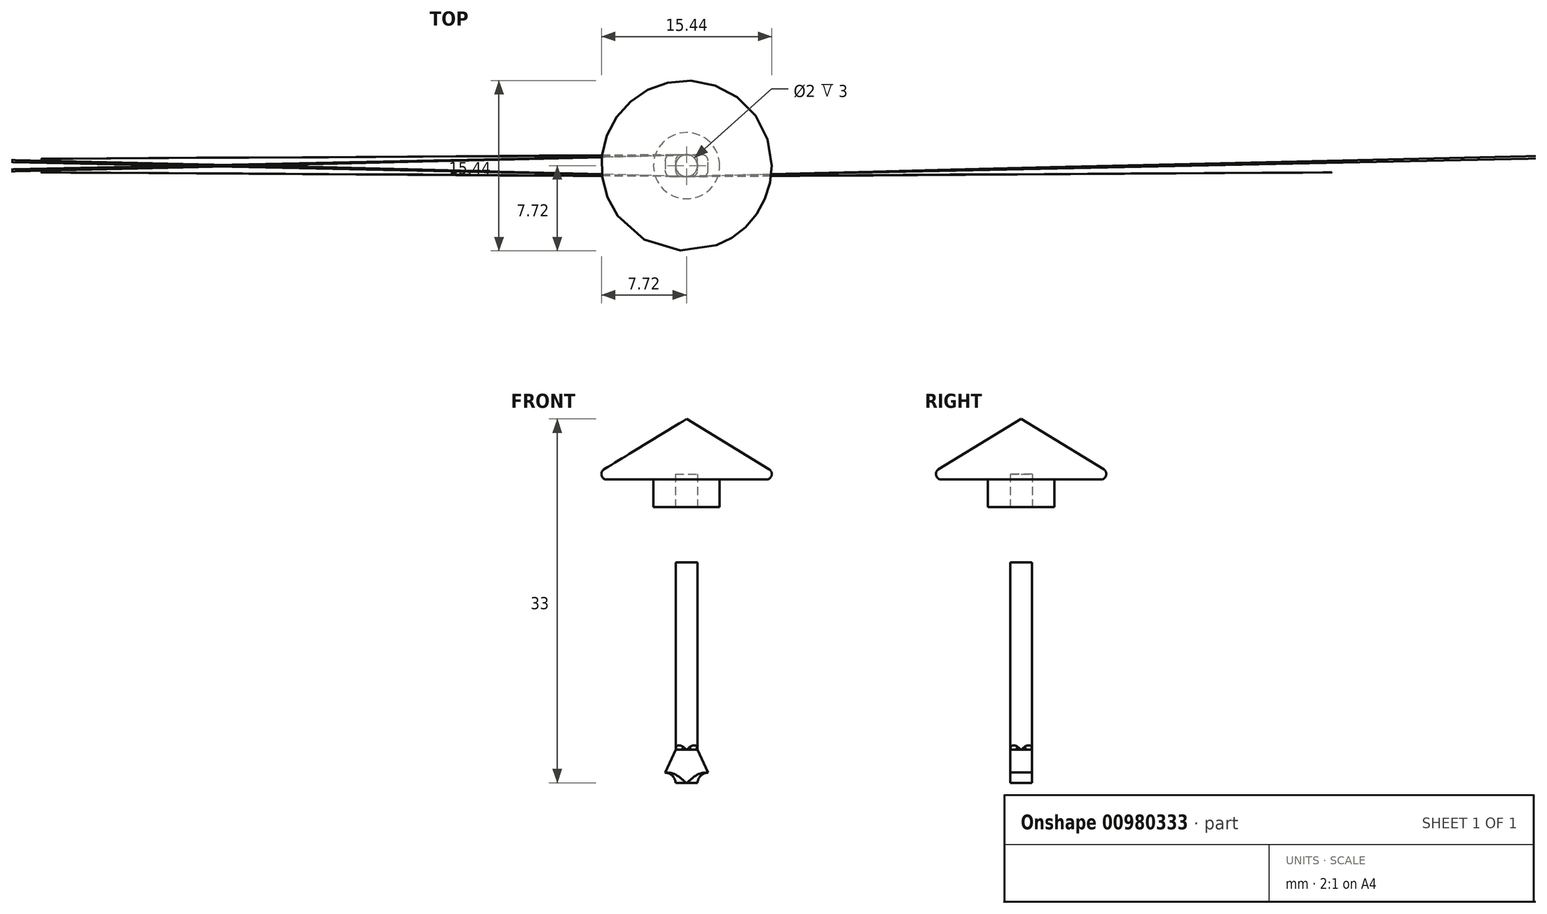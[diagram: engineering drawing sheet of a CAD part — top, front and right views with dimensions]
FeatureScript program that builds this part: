
annotation { "Feature Type Name" : "Feature", "Feature Type Description" : "" }
export const myFeature = defineFeature(function(context is Context, id is Id, definition is map)
    precondition{}
    {
        {
            var Q0;
            Q0=qCreatedBy(makeId("Front.planeOp"),FACE);
            var sketch = newSketch(context, id + "F0", { "sketchPlane" : qUnion([Q0])});
            skLineSegment(sketch, "E0", {"start": v(0, 8) * mm, "end": v(-9, 2.5) * mm});
            skLineSegment(sketch, "E1", {"start": v(-9, 2.5) * mm, "end": v(-3, 2.5) * mm});
            skLineSegment(sketch, "E2", {"start": v(-3, 2.5) * mm, "end": v(-3, 0) * mm});
            skLineSegment(sketch, "E3", {"start": v(-3, 0) * mm, "end": v(0, 0) * mm});
            skLineSegment(sketch, "E4", {"start": v(0, 0) * mm, "end": v(0, 8) * mm});
            skSolve(sketch);
        }
        {
            var Q0;
            Q0=makeQuery(id+"F0.imprint","IMPRINT",FACE,{"disambiguationData":[TD([[makeQuery(id+"F0.imprint","IMPRINT",EDGE,{"derivedFrom":sQuery(id+"F0.wireOp",EDGE,"E0")}),1.0]])]});
            var Q1;
            Q1=sQuery(id+"F0.wireOp",EDGE,"E4");
            revolve(context, id + "F1", {"surfaceOperationType" : NewSurfaceOperationType.NEW, "entities" : qUnion([Q0]), "axis" : qUnion([Q1]), "revolveType" : RevolveType.FULL});
        }
        {
            var Q0;
            Q0=makeQuery(id+"F1.opRevolve","SWEPT_EDGE",EDGE,{"disambiguationData":[OSD([sQuery(id+"F0.wireOp",EDGE,"E0"),sQuery(id+"F0.wireOp",EDGE,"E1")])]});
            var Q1;
            Q1=makeQuery(id+"F1.opRevolve","SWEPT_FACE",FACE,{"disambiguationData":[OSD([sQuery(id+"F0.wireOp",EDGE,"E0")])]});
            fillet(context, id + "F2", {"entities" : qUnion([Q0, Q1]), "radius" : 0.5 * mm, "tangentPropagation" : true, "allowEdgeOverflow" : false});
        }
        {
            var Q0;
            Q0=makeQuery(id+"F1.opRevolve","SWEPT_FACE",FACE,{"disambiguationData":[OSD([sQuery(id+"F0.wireOp",EDGE,"E3")])]});
            var sketch = newSketch(context, id + "F3", { "sketchPlane" : qUnion([Q0])});
            skCircle(sketch, "E5", {"center": v(0, 0) * mm, "radius": 1 * mm});
            skSolve(sketch);
        }
        {
            var Q0;
            Q0=makeQuery(id+"F3.imprint","IMPRINT",FACE,{"disambiguationData":[TD([[makeQuery(id+"F3.imprint","IMPRINT",EDGE,{"derivedFrom":sQuery(id+"F3.wireOp",EDGE,"E5")}),1.0]])]});
            extrude(context, id + "F4", {"entities" : qUnion([Q0]), "operationType" : NewBodyOperationType.REMOVE, "oppositeDirection" : true, "depth" : 3 * mm, "offsetDistance" : 25 * mm});
        }
        {
            var Q0;
            Q0=makeQuery(id+"F3.imprint","IMPRINT",FACE,{"disambiguationData":[TD([[makeQuery(id+"F3.imprint","IMPRINT",EDGE,{"derivedFrom":sQuery(id+"F3.wireOp",EDGE,"E5")}),-1.0]])]});
            cPlane(context, id + "F5", {"entities" : qUnion([Q0]), "cplaneType" : CPlaneType.OFFSET, "offset" : 5 * mm, "width" : 150 * mm, "height" : 150 * mm});
        }
        {
            var Q0;
            Q0=qCreatedBy(id+"F5.planeOp",FACE);
            var sketch = newSketch(context, id + "F6", { "sketchPlane" : qUnion([Q0])});
            skCircle(sketch, "E6", {"center": v(0, 0) * mm, "radius": 0.99 * mm});
            skSolve(sketch);
        }
        {
            var Q0;
            Q0 = qSketchRegion(id + "F6", true);
            extrude(context, id + "F7", {"entities" : qUnion([Q0]), "depth" : 20 * mm, "offsetDistance" : 25 * mm});
        }
        {
            var Q0;
            Q0=qCreatedBy(makeId("Front.planeOp"),FACE);
            var sketch = newSketch(context, id + "F8", { "sketchPlane" : qUnion([Q0])});
            skLineSegment(sketch, "E7", {"start": v(1, -5) * mm, "end": v(1, -25) * mm});
            skLineSegment(sketch, "E8", {"start": v(-0.99, -25) * mm, "end": v(-0.99, -5) * mm});
            skLineSegment(sketch, "E9", {"start": v(-0.99, -22) * mm, "end": v(-1.94, -24.07) * mm});
            skLineSegment(sketch, "E10", {"start": v(-1.94, -24.07) * mm, "end": v(1.94, -24.07) * mm});
            skLineSegment(sketch, "E11", {"start": v(1.94, -24.07) * mm, "end": v(1, -22) * mm});
            skLineSegment(sketch, "E12", {"start": v(0, -23.12) * mm, "end": v(0, -19.68) * mm, "construction": true});
            skLineSegment(sketch, "E13", {"start": v(-0.99, -22) * mm, "end": v(1, -22) * mm});
            skLineSegment(sketch, "E14.0", {"start": v(1, -5) * mm, "end": v(-0.99, -5) * mm});
            skLineSegment(sketch, "E15", {"start": v(-0.99, -25) * mm, "end": v(1, -25) * mm});
            skLineSegment(sketch, "E16", {"start": v(-0.99, -5) * mm, "end": v(1, -5) * mm});
            skSolve(sketch);
        }
        {
            var Q0;
            {var subQ0=sQuery(id+"F8.wireOp",EDGE,"E11");Q0=makeQuery(id+"F8.imprint","IMPRINT",FACE,{"disambiguationData":[TD([[makeQuery(id+"F8.imprint","IMPRINT",EDGE,{"derivedFrom":subQ0}),1.0]])]});}
            var Q1;
            {var subQ0=sQuery(id+"F8.wireOp",EDGE,"E13");Q1=makeQuery(id+"F8.imprint","IMPRINT",FACE,{"disambiguationData":[TD([[makeQuery(id+"F8.imprint","IMPRINT",EDGE,{"derivedFrom":subQ0}),-1.0]])]});}
            var Q2;
            {var subQ0=sQuery(id+"F8.wireOp",EDGE,"E9");Q2=makeQuery(id+"F8.imprint","IMPRINT",FACE,{"disambiguationData":[TD([[makeQuery(id+"F8.imprint","IMPRINT",EDGE,{"derivedFrom":subQ0}),1.0]])]});}
            extrude(context, id + "F9", {"entities" : qUnion([Q0, Q1, Q2]), "operationType" : NewBodyOperationType.ADD, "endBound" : BoundingType.SYMMETRIC, "depth" : 1.98 * mm, "offsetDistance" : 25 * mm});
        }
        {
            var Q0;
            Q0=makeQuery(id+"F9.opExtrude","CAP_EDGE",EDGE,{"disambiguationData":[OSD([sQuery(id+"F8.wireOp",EDGE,"E11")])],"isStart":false});
            var Q1;
            Q1=makeQuery(id+"F9.opExtrude","CAP_EDGE",EDGE,{"disambiguationData":[OSD([sQuery(id+"F8.wireOp",EDGE,"E9")])],"isStart":false});
            var Q2;
            Q2=makeQuery(id+"F9.opExtrude","CAP_EDGE",EDGE,{"disambiguationData":[OSD([sQuery(id+"F8.wireOp",EDGE,"E9")])],"isStart":true});
            var Q3;
            Q3=makeQuery(id+"F9.opExtrude","CAP_EDGE",EDGE,{"disambiguationData":[OSD([sQuery(id+"F8.wireOp",EDGE,"E11")])],"isStart":true});
            fillet(context, id + "F10", {"entities" : qUnion([Q0, Q1, Q2, Q3]), "radius" : 0.5 * mm, "tangentPropagation" : true, "allowEdgeOverflow" : false});
        }
        {
            var Q0;
            Q0=makeQuery(id+"F9.boolean.opBoolean","INTERSECT",EDGE,{"disambiguationData":[OD(2.0)],"derivedFrom":[makeQuery(id+"F7.opExtrude","SWEPT_FACE",FACE,{"disambiguationData":[OSD([sQuery(id+"F6.wireOp",EDGE,"E6")])]}),makeQuery(id+"F9.opExtrude","SWEPT_FACE",FACE,{"disambiguationData":[OSD([sQuery(id+"F8.wireOp",EDGE,"E13")])]})]});
            var Q1;
            Q1=makeQuery(id+"F9.boolean.opBoolean","INTERSECT",EDGE,{"disambiguationData":[OD(3.0)],"derivedFrom":[makeQuery(id+"F7.opExtrude","SWEPT_FACE",FACE,{"disambiguationData":[OSD([sQuery(id+"F6.wireOp",EDGE,"E6")])]}),makeQuery(id+"F9.opExtrude","SWEPT_FACE",FACE,{"disambiguationData":[OSD([sQuery(id+"F8.wireOp",EDGE,"E13")])]})]});
            var Q2;
            Q2=makeQuery(id+"F9.boolean.opBoolean","INTERSECT",EDGE,{"disambiguationData":[OD(0.0)],"derivedFrom":[makeQuery(id+"F7.opExtrude","SWEPT_FACE",FACE,{"disambiguationData":[OSD([sQuery(id+"F6.wireOp",EDGE,"E6")])]}),makeQuery(id+"F9.opExtrude","SWEPT_FACE",FACE,{"disambiguationData":[OSD([sQuery(id+"F8.wireOp",EDGE,"E13")])]})]});
            var Q3;
            Q3=makeQuery(id+"F9.boolean.opBoolean","INTERSECT",EDGE,{"disambiguationData":[OD(1.0)],"derivedFrom":[makeQuery(id+"F7.opExtrude","SWEPT_FACE",FACE,{"disambiguationData":[OSD([sQuery(id+"F6.wireOp",EDGE,"E6")])]}),makeQuery(id+"F9.opExtrude","SWEPT_FACE",FACE,{"disambiguationData":[OSD([sQuery(id+"F8.wireOp",EDGE,"E13")])]})]});
            fillet(context, id + "F11", {"entities" : qUnion([Q0, Q1, Q2, Q3]), "radius" : 0.5 * mm, "tangentPropagation" : true, "allowEdgeOverflow" : false});
        }
        {
            var Q0;
            Q0=makeQuery(id+"F9.boolean.opBoolean","INTERSECT",EDGE,{"disambiguationData":[OD(1.0)],"derivedFrom":[makeQuery(id+"F7.opExtrude","SWEPT_FACE",FACE,{"disambiguationData":[OSD([sQuery(id+"F6.wireOp",EDGE,"E6")])]}),makeQuery(id+"F9.opExtrude","SWEPT_FACE",FACE,{"disambiguationData":[OSD([sQuery(id+"F8.wireOp",EDGE,"E10")])]})]});
            var Q1;
            Q1=makeQuery(id+"F9.boolean.opBoolean","INTERSECT",EDGE,{"disambiguationData":[OD(0.0)],"derivedFrom":[makeQuery(id+"F7.opExtrude","SWEPT_FACE",FACE,{"disambiguationData":[OSD([sQuery(id+"F6.wireOp",EDGE,"E6")])]}),makeQuery(id+"F9.opExtrude","SWEPT_FACE",FACE,{"disambiguationData":[OSD([sQuery(id+"F8.wireOp",EDGE,"E10")])]})]});
            fillet(context, id + "F12", {"entities" : qUnion([Q0, Q1]), "radius" : 1 * mm, "tangentPropagation" : true, "allowEdgeOverflow" : false});
        }
    });
